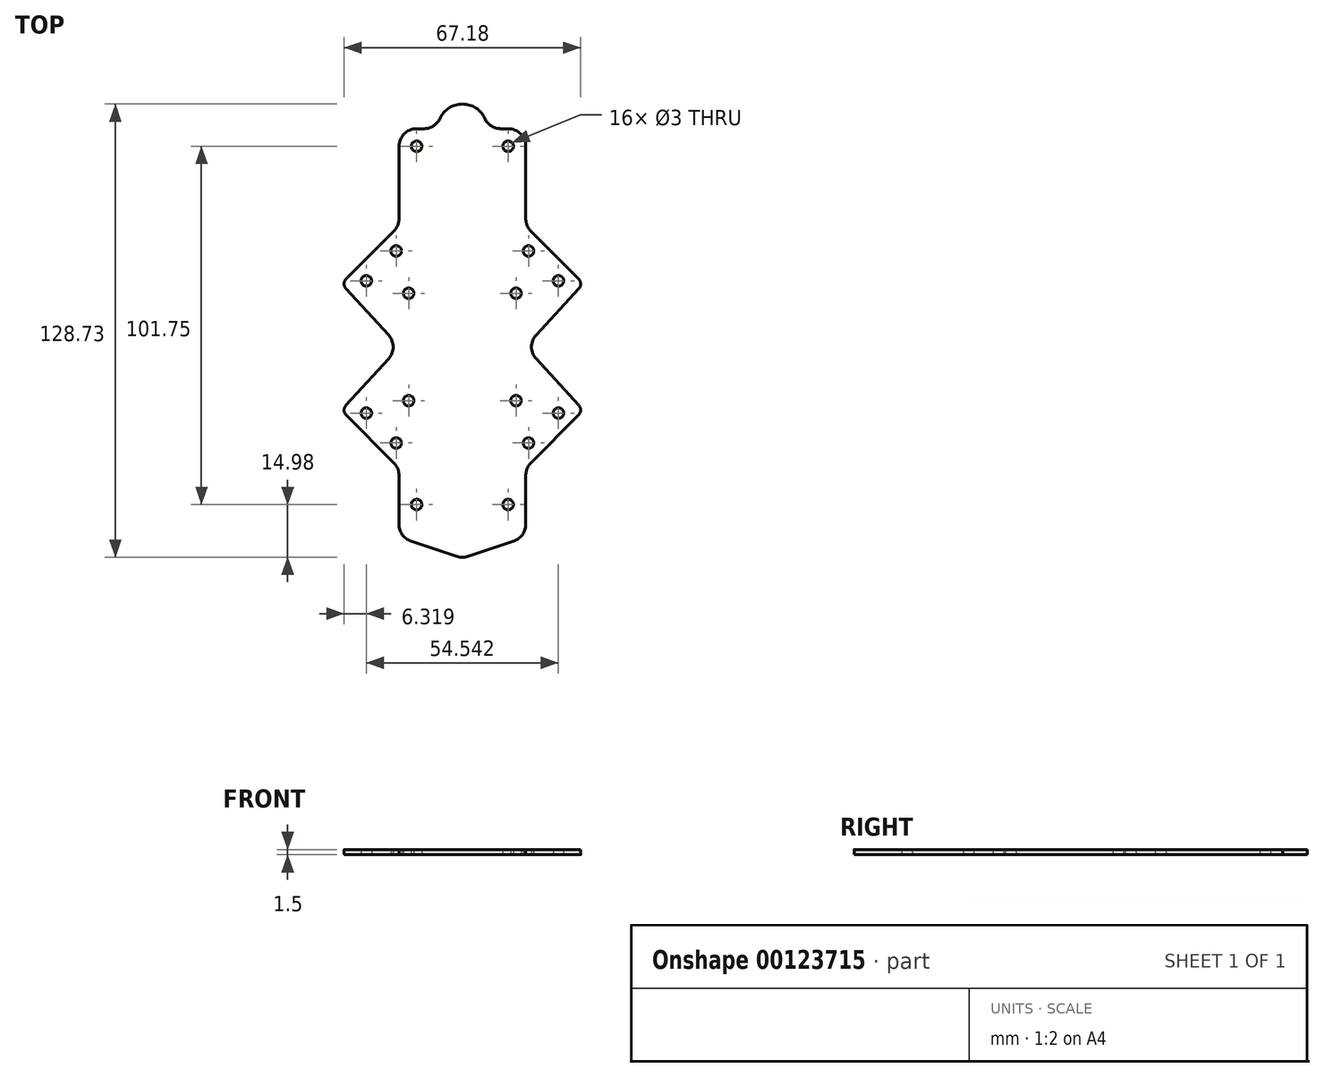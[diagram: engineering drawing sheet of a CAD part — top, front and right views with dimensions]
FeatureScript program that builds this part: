
annotation { "Feature Type Name" : "Feature", "Feature Type Description" : "" }
export const myFeature = defineFeature(function(context is Context, id is Id, definition is map)
    precondition{}
    {
        {
            var Q0;
            Q0=qCreatedBy(makeId("Top.planeOp"),FACE);
            var sketch = newSketch(context, id + "F0", { "sketchPlane" : qUnion([Q0])});
            skCircle(sketch, "E0", {"center": v(-15.25, 15.25) * mm, "radius": 1.5 * mm});
            skCircle(sketch, "E1.0.1.0", {"center": v(-15.25, -15.25) * mm, "radius": 1.5 * mm});
            skCircle(sketch, "E1.1.0.0", {"center": v(15.25, 15.25) * mm, "radius": 1.5 * mm});
            skCircle(sketch, "E1.1.1.0", {"center": v(15.25, -15.25) * mm, "radius": 1.5 * mm});
            skLineSegment(sketch, "E1.direction1", {"start": v(-15.25, 15.25) * mm, "end": v(15.25, 15.25) * mm, "construction": true});
            skLineSegment(sketch, "E1.direction2", {"start": v(-15.25, 15.25) * mm, "end": v(-15.25, -15.25) * mm, "construction": true});
            skLineSegment(sketch, "E2", {"start": v(-42.43, -42.43) * mm, "end": v(42.43, 42.43) * mm, "construction": true});
            skLineSegment(sketch, "E3", {"start": v(-42.43, 42.43) * mm, "end": v(42.43, -42.43) * mm, "construction": true});
            skPoint(sketch, "E4.endSnap0", {"position": v(0, 15.25) * mm});
            skLineSegment(sketch, "E5", {"start": v(20.96, -3.38) * mm, "end": v(34.36, -18) * mm});
            skLineSegment(sketch, "E6", {"start": v(-20.96, 3.38) * mm, "end": v(-34.36, 18) * mm});
            skLineSegment(sketch, "E7", {"start": v(-27.27, 18.79) * mm, "end": v(-18.79, 27.27) * mm, "construction": true});
            skLineSegment(sketch, "E8", {"start": v(18.79, 27.27) * mm, "end": v(27.27, 18.79) * mm, "construction": true});
            skLineSegment(sketch, "E9", {"start": v(-27.27, -18.79) * mm, "end": v(-18.79, -27.27) * mm, "construction": true});
            skLineSegment(sketch, "E10", {"start": v(18.79, -27.27) * mm, "end": v(27.27, -18.79) * mm, "construction": true});
            skCircle(sketch, "E11", {"center": v(-27.27, -18.79) * mm, "radius": 1.5 * mm});
            skCircle(sketch, "E12", {"center": v(-18.79, -27.27) * mm, "radius": 1.5 * mm});
            skCircle(sketch, "E13", {"center": v(18.79, -27.27) * mm, "radius": 1.5 * mm});
            skCircle(sketch, "E14", {"center": v(27.27, -18.79) * mm, "radius": 1.5 * mm});
            skCircle(sketch, "E15", {"center": v(27.27, 18.79) * mm, "radius": 1.5 * mm});
            skCircle(sketch, "E16", {"center": v(18.79, 27.27) * mm, "radius": 1.5 * mm});
            skCircle(sketch, "E17", {"center": v(-18.79, 27.27) * mm, "radius": 1.5 * mm});
            skCircle(sketch, "E18", {"center": v(-27.27, 18.79) * mm, "radius": 1.5 * mm});
            skPoint(sketch, "E19.orphan", {"position": v(-17.86, 0) * mm});
            skArc(sketch, "E20", {"start": v(20.96, 3.38) * mm, "mid": v(19.65, 0) * mm, "end": v(20.96, -3.38) * mm});
            skPoint(sketch, "E21.orphan", {"position": v(17.86, 0) * mm});
            skArc(sketch, "E22", {"start": v(-20.96, -3.38) * mm, "mid": v(-19.65, 0) * mm, "end": v(-20.96, 3.38) * mm});
            skLineSegment(sketch, "E23", {"start": v(-13, -44.75) * mm, "end": v(13, -44.75) * mm, "construction": true});
            skCircle(sketch, "E24", {"center": v(-13, -44.75) * mm, "radius": 1.5 * mm});
            skCircle(sketch, "E25", {"center": v(13, -44.75) * mm, "radius": 1.5 * mm});
            skLineSegment(sketch, "E26", {"start": v(-20, -40.25) * mm, "end": v(20, -40.25) * mm, "construction": true});
            skLineSegment(sketch, "E27", {"start": v(-18, -34.36) * mm, "end": v(-18, -54) * mm});
            skLineSegment(sketch, "E28", {"start": v(18, -34.36) * mm, "end": v(18, -54) * mm});
            skLineSegment(sketch, "E29", {"start": v(-18, 34.36) * mm, "end": v(-18, 62) * mm});
            skLineSegment(sketch, "E30", {"start": v(18, 34.36) * mm, "end": v(18, 62) * mm});
            skLineSegment(sketch, "E31", {"start": v(-18, 62) * mm, "end": v(-10.9, 62) * mm});
            skLineSegment(sketch, "E32", {"start": v(-18, -54) * mm, "end": v(18, -54) * mm, "construction": true});
            skLineSegment(sketch, "E33", {"start": v(-18, -54) * mm, "end": v(0, -60) * mm});
            skLineSegment(sketch, "E34", {"start": v(0, -60) * mm, "end": v(18, -54) * mm});
            skCircle(sketch, "E35", {"center": v(0, 0) * mm, "radius": 110 * mm, "construction": true});
            skLineSegment(sketch, "E36", {"start": v(42.43, 42.43) * mm, "end": v(77.78, 77.78) * mm, "construction": true});
            skLineSegment(sketch, "E37", {"start": v(-42.43, 42.43) * mm, "end": v(-77.78, 77.78) * mm, "construction": true});
            skLineSegment(sketch, "E38", {"start": v(-42.43, -42.43) * mm, "end": v(-77.78, -77.78) * mm, "construction": true});
            skLineSegment(sketch, "E39", {"start": v(42.43, -42.43) * mm, "end": v(77.78, -77.78) * mm, "construction": true});
            skCircle(sketch, "E40", {"center": v(-77.78, 77.78) * mm, "radius": 63.5 * mm, "construction": true});
            skCircle(sketch, "E41", {"center": v(-77.78, -77.78) * mm, "radius": 63.5 * mm, "construction": true});
            skCircle(sketch, "E42", {"center": v(77.78, 77.78) * mm, "radius": 63.5 * mm, "construction": true});
            skCircle(sketch, "E43", {"center": v(77.78, -77.78) * mm, "radius": 63.5 * mm, "construction": true});
            skCircle(sketch, "E44", {"center": v(-13, 57) * mm, "radius": 1.5 * mm});
            skCircle(sketch, "E45", {"center": v(13, 57) * mm, "radius": 1.5 * mm});
            skArc(sketch, "E46", {"start": v(6.36, 64.92) * mm, "mid": v(0, 69) * mm, "end": v(-6.36, 64.92) * mm});
            skLineSegment(sketch, "E47.trimOffspring", {"start": v(10.9, 62) * mm, "end": v(18, 62) * mm});
            skPoint(sketch, "E48.visualSharp", {"position": v(-7, 62) * mm});
            skArc(sketch, "E48.filletArc", {"start": v(-10.9, 62) * mm, "mid": v(-8.2, 62.8) * mm, "end": v(-6.36, 64.92) * mm});
            skPoint(sketch, "E49.visualSharp", {"position": v(7, 62) * mm});
            skArc(sketch, "E49.filletArc", {"start": v(6.36, 64.92) * mm, "mid": v(8.2, 62.8) * mm, "end": v(10.9, 62) * mm});
            skLineSegment(sketch, "E50", {"start": v(18, 34.36) * mm, "end": v(34.36, 18) * mm});
            skLineSegment(sketch, "E51.trimOffspring", {"start": v(34.36, 18) * mm, "end": v(20.96, 3.38) * mm});
            skLineSegment(sketch, "E52", {"start": v(-18, -34.36) * mm, "end": v(-34.36, -18) * mm});
            skLineSegment(sketch, "E53.trimOffspring", {"start": v(-34.36, -18) * mm, "end": v(-20.96, -3.38) * mm});
            skLineSegment(sketch, "E54", {"start": v(18, -34.36) * mm, "end": v(34.36, -18) * mm});
            skLineSegment(sketch, "E55", {"start": v(-18, 34.36) * mm, "end": v(-34.36, 18) * mm});
            skSolve(sketch);
        }
        {
            var Q0;
            Q0=qSketchRegion(id+"F0",true);
            extrude(context, id + "F1", {"entities" : qUnion([Q0]), "depth" : 1.5 * mm});
        }
        {
            var Q0;
            Q0=makeQuery(id+"F1.opExtrude","SWEPT_EDGE",EDGE,{"disambiguationData":[OSD([sQuery(id+"F0.wireOp",EDGE,"E27"),sQuery(id+"F0.wireOp",EDGE,"E33")])]});
            var Q1;
            Q1=makeQuery(id+"F1.opExtrude","SWEPT_EDGE",EDGE,{"disambiguationData":[OSD([sQuery(id+"F0.wireOp",EDGE,"E33"),sQuery(id+"F0.wireOp",EDGE,"E34")])]});
            var Q2;
            Q2=makeQuery(id+"F1.opExtrude","SWEPT_EDGE",EDGE,{"disambiguationData":[OSD([sQuery(id+"F0.wireOp",EDGE,"E28"),sQuery(id+"F0.wireOp",EDGE,"E34")])]});
            var Q3;
            Q3=makeQuery(id+"F1.opExtrude","SWEPT_EDGE",EDGE,{"disambiguationData":[OSD([sQuery(id+"F0.wireOp",EDGE,"E30"),sQuery(id+"F0.wireOp",EDGE,"E31")])]});
            var Q4;
            Q4=makeQuery(id+"F1.opExtrude","SWEPT_EDGE",EDGE,{"disambiguationData":[OSD([sQuery(id+"F0.wireOp",EDGE,"E29"),sQuery(id+"F0.wireOp",EDGE,"E31")])]});
            var Q5;
            Q5=makeQuery(id+"F1.opExtrude","SWEPT_EDGE",EDGE,{"disambiguationData":[OSD([sQuery(id+"F0.wireOp",EDGE,"8RzHtvJp-6ahc-jpdW-AccZ-miNvszTl99jN"),sQuery(id+"F0.wireOp",EDGE,"E30")])]});
            var Q6;
            Q6=makeQuery(id+"F1.opExtrude","SWEPT_EDGE",EDGE,{"disambiguationData":[OSD([sQuery(id+"F0.wireOp",EDGE,"yWU6gNeh-TWqC-plX3-D1ue-xNKcKi38tUiX"),sQuery(id+"F0.wireOp",EDGE,"E28")])]});
            var Q7;
            Q7=makeQuery(id+"F1.opExtrude","SWEPT_EDGE",EDGE,{"disambiguationData":[OSD([sQuery(id+"F0.wireOp",EDGE,"koecdbpq-Kg7q-WjNf-1vjh-WAGrbZ8yPwAs"),sQuery(id+"F0.wireOp",EDGE,"E27")])]});
            var Q8;
            Q8=makeQuery(id+"F1.opExtrude","SWEPT_EDGE",EDGE,{"disambiguationData":[OSD([sQuery(id+"F0.wireOp",EDGE,"E4"),sQuery(id+"F0.wireOp",EDGE,"E29")])]});
            fillet(context, id + "F2", {"entities" : qUnion([Q0, Q1, Q2, Q3, Q4, Q5, Q6, Q7, Q8]), "radius" : 5 * mm, "tangentPropagation" : true, "allowEdgeOverflow" : false});
        }
        {
            var Q0;
            Q0=makeQuery(id+"F1.opExtrude","SWEPT_EDGE",EDGE,{"disambiguationData":[OSD([sQuery(id+"F0.wireOp",EDGE,"E52"),sQuery(id+"F0.wireOp",EDGE,"E53.trimOffspring")])]});
            var Q1;
            Q1=makeQuery(id+"F1.opExtrude","SWEPT_EDGE",EDGE,{"disambiguationData":[OSD([sQuery(id+"F0.wireOp",EDGE,"E6"),sQuery(id+"F0.wireOp",EDGE,"E55")])]});
            var Q2;
            Q2=makeQuery(id+"F1.opExtrude","SWEPT_EDGE",EDGE,{"disambiguationData":[OSD([sQuery(id+"F0.wireOp",EDGE,"E50"),sQuery(id+"F0.wireOp",EDGE,"E51.trimOffspring")])]});
            var Q3;
            Q3=makeQuery(id+"F1.opExtrude","SWEPT_EDGE",EDGE,{"disambiguationData":[OSD([sQuery(id+"F0.wireOp",EDGE,"E5"),sQuery(id+"F0.wireOp",EDGE,"E54")])]});
            fillet(context, id + "F3", {"entities" : qUnion([Q0, Q1, Q2, Q3]), "radius" : 2 * mm, "tangentPropagation" : true, "allowEdgeOverflow" : false});
        }
    });
